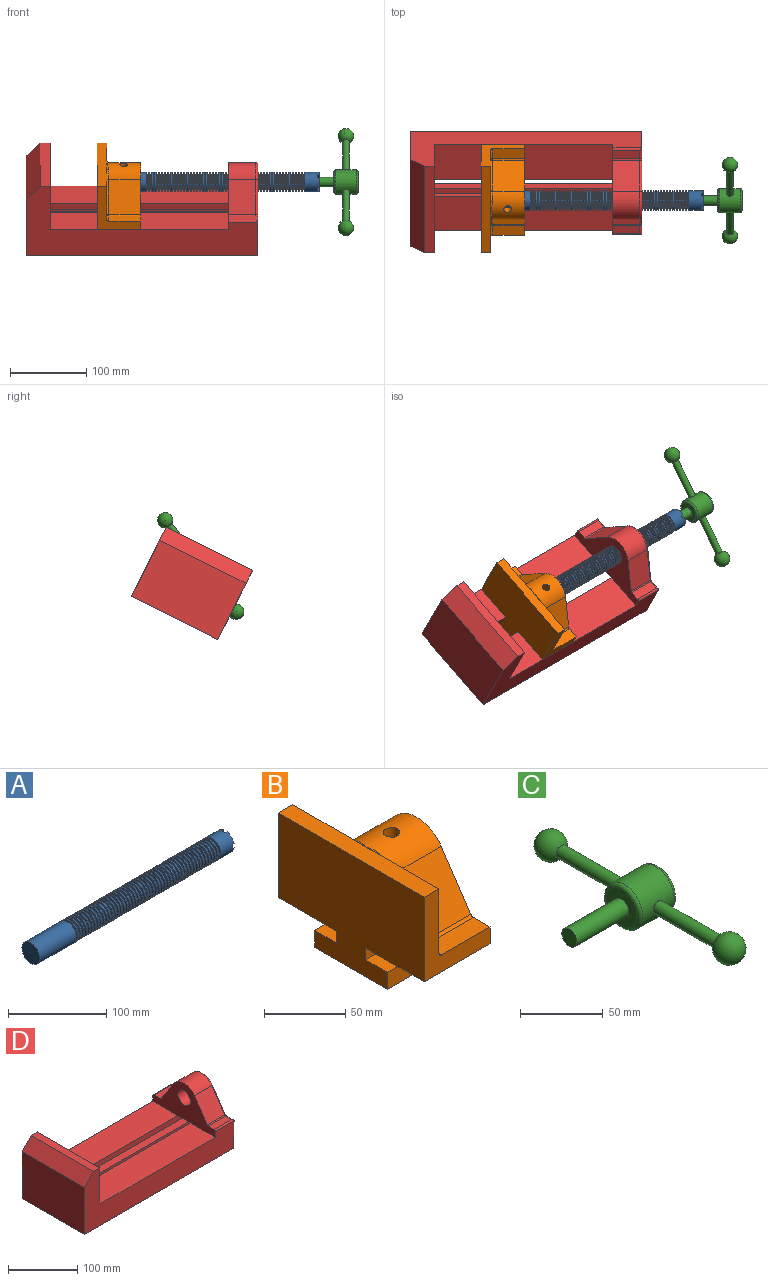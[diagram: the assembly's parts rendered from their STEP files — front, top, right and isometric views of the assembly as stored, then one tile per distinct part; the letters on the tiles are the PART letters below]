
ASSEMBLY  parts=4 mates=3
PART A: 220 faces, bbox 279.4x25.4x25.4 mm
  f0: cylinder r=12.7mm len=25.4mm, axis (-1,0,0), area 1468.2mm2, adj f1,f2,f3,f5,f7,f208,f209,f210
  f1: plane 9.9x9.9mm, normal (1,0,0), area 62.3mm2, adj f0,f4,f213,f216
  f2: plane 9.9x9.9mm, normal (1,0,0), area 62.3mm2, adj f0,f4,f210,f218
  f3: plane 9.9x9.9mm, normal (1,0,0), area 62.3mm2, adj f0,f4,f209,f212
  f4: cylinder r=6.35mm len=25.4mm, axis (1,0,0), area 960.3mm2, adj f1,f2,f3,f5,f6,f208,f209,f210
  f5: plane 9.9x9.9mm, normal (1,0,0), area 62.3mm2, adj f0,f4,f215,f217
  f6: plane 12.7x12.7mm, normal (1,0,0), area 126.7mm2, adj f4
  f7: cone r=12.7mm half-angle=76deg, axis (1,0,0), area 188mm2, adj f0,f9
  f8: cone r=10.16mm half-angle=76deg, axis (-1,0,0), area 188mm2, adj f9,f10
  f9: cylinder r=10.16mm len=20.32mm, axis (1,0,0), area 81.1mm2, adj f7,f8
  f10: cylinder r=12.7mm len=25.4mm, axis (-1,0,0), area 131.7mm2, adj f8,f11
  f11: cone r=12.7mm half-angle=76deg, axis (1,0,0), area 188mm2, adj f10,f13
  f12: cone r=10.16mm half-angle=76deg, axis (-1,0,0), area 188mm2, adj f13,f14
  f13: cylinder r=10.16mm len=20.32mm, axis (1,0,0), area 81.1mm2, adj f11,f12
  f14: cylinder r=12.7mm len=25.4mm, axis (-1,0,0), area 131.7mm2, adj f12,f15
  f15: cone r=12.7mm half-angle=76deg, axis (1,0,0), area 188mm2, adj f14,f17
  f16: cone r=10.16mm half-angle=76deg, axis (-1,0,0), area 188mm2, adj f17,f18
  f17: cylinder r=10.16mm len=20.32mm, axis (1,0,0), area 81.1mm2, adj f15,f16
  f18: cylinder r=12.7mm len=25.4mm, axis (-1,0,0), area 131.7mm2, adj f16,f19
  f19: cone r=12.7mm half-angle=76deg, axis (1,0,0), area 188mm2, adj f18,f21
  f20: cone r=10.16mm half-angle=76deg, axis (-1,0,0), area 188mm2, adj f21,f22
  f21: cylinder r=10.16mm len=20.32mm, axis (1,0,0), area 81.1mm2, adj f19,f20
  f22: cylinder r=12.7mm len=25.4mm, axis (-1,0,0), area 131.7mm2, adj f20,f23
  f23: cone r=12.7mm half-angle=76deg, axis (1,0,0), area 188mm2, adj f22,f25
  f24: cone r=10.16mm half-angle=76deg, axis (-1,0,0), area 188mm2, adj f25,f26
  f25: cylinder r=10.16mm len=20.32mm, axis (1,0,0), area 81.1mm2, adj f23,f24
  f26: cylinder r=12.7mm len=25.4mm, axis (-1,0,0), area 131.7mm2, adj f24,f27
  f27: cone r=12.7mm half-angle=76deg, axis (1,0,0), area 188mm2, adj f26,f29
  f28: cone r=10.16mm half-angle=76deg, axis (-1,0,0), area 188mm2, adj f29,f30
  f29: cylinder r=10.16mm len=20.32mm, axis (1,0,0), area 81.1mm2, adj f27,f28
  f30: cylinder r=12.7mm len=25.4mm, axis (-1,0,0), area 131.7mm2, adj f28,f31
  f31: cone r=12.7mm half-angle=76deg, axis (1,0,0), area 188mm2, adj f30,f33
  f32: cone r=10.16mm half-angle=76deg, axis (-1,0,0), area 188mm2, adj f33,f34
  f33: cylinder r=10.16mm len=20.32mm, axis (1,0,0), area 81.1mm2, adj f31,f32
  f34: cylinder r=12.7mm len=25.4mm, axis (-1,0,0), area 131.7mm2, adj f32,f35
  f35: cone r=12.7mm half-angle=76deg, axis (1,0,0), area 188mm2, adj f34,f37
  f36: cone r=10.16mm half-angle=76deg, axis (-1,0,0), area 188mm2, adj f37,f38
  f37: cylinder r=10.16mm len=20.32mm, axis (1,0,0), area 81.1mm2, adj f35,f36
  f38: cylinder r=12.7mm len=25.4mm, axis (-1,0,0), area 131.7mm2, adj f36,f39
  f39: cone r=12.7mm half-angle=76deg, axis (1,0,0), area 188mm2, adj f38,f41
  f40: cone r=10.16mm half-angle=76deg, axis (-1,0,0), area 188mm2, adj f41,f42
  f41: cylinder r=10.16mm len=20.32mm, axis (1,0,0), area 81.1mm2, adj f39,f40
  f42: cylinder r=12.7mm len=25.4mm, axis (-1,0,0), area 131.7mm2, adj f40,f43
  f43: cone r=12.7mm half-angle=76deg, axis (1,0,0), area 188mm2, adj f42,f45
  f44: cone r=10.16mm half-angle=76deg, axis (-1,0,0), area 188mm2, adj f45,f46
  f45: cylinder r=10.16mm len=20.32mm, axis (1,0,0), area 81.1mm2, adj f43,f44
  f46: cylinder r=12.7mm len=25.4mm, axis (-1,0,0), area 131.7mm2, adj f44,f47
  f47: cone r=12.7mm half-angle=76deg, axis (1,0,0), area 188mm2, adj f46,f49
  f48: cone r=10.16mm half-angle=76deg, axis (-1,0,0), area 188mm2, adj f49,f50
  f49: cylinder r=10.16mm len=20.32mm, axis (1,0,0), area 81.1mm2, adj f47,f48
  f50: cylinder r=12.7mm len=25.4mm, axis (-1,0,0), area 131.7mm2, adj f48,f51
  f51: cone r=12.7mm half-angle=76deg, axis (1,0,0), area 188mm2, adj f50,f53
  f52: cone r=10.16mm half-angle=76deg, axis (-1,0,0), area 188mm2, adj f53,f54
  f53: cylinder r=10.16mm len=20.32mm, axis (1,0,0), area 81.1mm2, adj f51,f52
  f54: cylinder r=12.7mm len=25.4mm, axis (-1,0,0), area 131.7mm2, adj f52,f55
  f55: cone r=12.7mm half-angle=76deg, axis (1,0,0), area 188mm2, adj f54,f57
  f56: cone r=10.16mm half-angle=76deg, axis (-1,0,0), area 188mm2, adj f57,f58
  f57: cylinder r=10.16mm len=20.32mm, axis (1,0,0), area 81.1mm2, adj f55,f56
  f58: cylinder r=12.7mm len=25.4mm, axis (-1,0,0), area 131.7mm2, adj f56,f59
  f59: cone r=12.7mm half-angle=76deg, axis (1,0,0), area 188mm2, adj f58,f61
  f60: cone r=10.16mm half-angle=76deg, axis (-1,0,0), area 188mm2, adj f61,f62
  f61: cylinder r=10.16mm len=20.32mm, axis (1,0,0), area 81.1mm2, adj f59,f60
  f62: cylinder r=12.7mm len=25.4mm, axis (-1,0,0), area 131.7mm2, adj f60,f63
  f63: cone r=12.7mm half-angle=76deg, axis (1,0,0), area 188mm2, adj f62,f65
  f64: cone r=10.16mm half-angle=76deg, axis (-1,0,0), area 188mm2, adj f65,f66
  f65: cylinder r=10.16mm len=20.32mm, axis (1,0,0), area 81.1mm2, adj f63,f64
  f66: cylinder r=12.7mm len=25.4mm, axis (-1,0,0), area 131.7mm2, adj f64,f67
  f67: cone r=12.7mm half-angle=76deg, axis (1,0,0), area 188mm2, adj f66,f69
  f68: cone r=10.16mm half-angle=76deg, axis (-1,0,0), area 188mm2, adj f69,f70
  f69: cylinder r=10.16mm len=20.32mm, axis (1,0,0), area 81.1mm2, adj f67,f68
  f70: cylinder r=12.7mm len=25.4mm, axis (-1,0,0), area 131.7mm2, adj f68,f71
  f71: cone r=12.7mm half-angle=76deg, axis (1,0,0), area 188mm2, adj f70,f73
  f72: cone r=10.16mm half-angle=76deg, axis (-1,0,0), area 188mm2, adj f73,f74
  f73: cylinder r=10.16mm len=20.32mm, axis (1,0,0), area 81.1mm2, adj f71,f72
  f74: cylinder r=12.7mm len=25.4mm, axis (-1,0,0), area 131.7mm2, adj f72,f75
  f75: cone r=12.7mm half-angle=76deg, axis (1,0,0), area 188mm2, adj f74,f77
  f76: cone r=10.16mm half-angle=76deg, axis (-1,0,0), area 188mm2, adj f77,f78
  f77: cylinder r=10.16mm len=20.32mm, axis (1,0,0), area 81.1mm2, adj f75,f76
  f78: cylinder r=12.7mm len=25.4mm, axis (-1,0,0), area 131.7mm2, adj f76,f79
  f79: cone r=12.7mm half-angle=76deg, axis (1,0,0), area 188mm2, adj f78,f81
  f80: cone r=10.16mm half-angle=76deg, axis (-1,0,0), area 188mm2, adj f81,f82
  f81: cylinder r=10.16mm len=20.32mm, axis (1,0,0), area 81.1mm2, adj f79,f80
  f82: cylinder r=12.7mm len=25.4mm, axis (-1,0,0), area 131.7mm2, adj f80,f83
  f83: cone r=12.7mm half-angle=76deg, axis (1,0,0), area 188mm2, adj f82,f85
  f84: cone r=10.16mm half-angle=76deg, axis (-1,0,0), area 188mm2, adj f85,f86
  f85: cylinder r=10.16mm len=20.32mm, axis (1,0,0), area 81.1mm2, adj f83,f84
  f86: cylinder r=12.7mm len=25.4mm, axis (-1,0,0), area 131.7mm2, adj f84,f87
  f87: cone r=12.7mm half-angle=76deg, axis (1,0,0), area 188mm2, adj f86,f89
  f88: cone r=10.16mm half-angle=76deg, axis (-1,0,0), area 188mm2, adj f89,f90
  f89: cylinder r=10.16mm len=20.32mm, axis (1,0,0), area 81.1mm2, adj f87,f88
  f90: cylinder r=12.7mm len=25.4mm, axis (-1,0,0), area 131.7mm2, adj f88,f91
  f91: cone r=12.7mm half-angle=76deg, axis (1,0,0), area 188mm2, adj f90,f93
  f92: cone r=10.16mm half-angle=76deg, axis (-1,0,0), area 188mm2, adj f93,f94
  f93: cylinder r=10.16mm len=20.32mm, axis (1,0,0), area 81.1mm2, adj f91,f92
  f94: cylinder r=12.7mm len=25.4mm, axis (-1,0,0), area 131.7mm2, adj f92,f95
  f95: cone r=12.7mm half-angle=76deg, axis (1,0,0), area 188mm2, adj f94,f97
  f96: cone r=10.16mm half-angle=76deg, axis (-1,0,0), area 188mm2, adj f97,f98
  f97: cylinder r=10.16mm len=20.32mm, axis (1,0,0), area 81.1mm2, adj f95,f96
  f98: cylinder r=12.7mm len=25.4mm, axis (-1,0,0), area 131.7mm2, adj f96,f99
  f99: cone r=12.7mm half-angle=76deg, axis (1,0,0), area 188mm2, adj f98,f101
  f100: cone r=10.16mm half-angle=76deg, axis (-1,0,0), area 188mm2, adj f101,f102
  f101: cylinder r=10.16mm len=20.32mm, axis (1,0,0), area 81.1mm2, adj f99,f100
  f102: cylinder r=12.7mm len=25.4mm, axis (-1,0,0), area 131.7mm2, adj f100,f103
  f103: cone r=12.7mm half-angle=76deg, axis (1,0,0), area 188mm2, adj f102,f105
  f104: cone r=10.16mm half-angle=76deg, axis (-1,0,0), area 188mm2, adj f105,f106
  f105: cylinder r=10.16mm len=20.32mm, axis (1,0,0), area 81.1mm2, adj f103,f104
  f106: cylinder r=12.7mm len=25.4mm, axis (-1,0,0), area 131.7mm2, adj f104,f107
  f107: cone r=12.7mm half-angle=76deg, axis (1,0,0), area 188mm2, adj f106,f109
  f108: cone r=10.16mm half-angle=76deg, axis (-1,0,0), area 188mm2, adj f109,f110
  f109: cylinder r=10.16mm len=20.32mm, axis (1,0,0), area 81.1mm2, adj f107,f108
  f110: cylinder r=12.7mm len=25.4mm, axis (-1,0,0), area 131.7mm2, adj f108,f111
  f111: cone r=12.7mm half-angle=76deg, axis (1,0,0), area 188mm2, adj f110,f113
  f112: cone r=10.16mm half-angle=76deg, axis (-1,0,0), area 188mm2, adj f113,f114
  f113: cylinder r=10.16mm len=20.32mm, axis (1,0,0), area 81.1mm2, adj f111,f112
  f114: cylinder r=12.7mm len=25.4mm, axis (-1,0,0), area 131.7mm2, adj f112,f115
  f115: cone r=12.7mm half-angle=76deg, axis (1,0,0), area 188mm2, adj f114,f117
  f116: cone r=10.16mm half-angle=76deg, axis (-1,0,0), area 188mm2, adj f117,f118
  f117: cylinder r=10.16mm len=20.32mm, axis (1,0,0), area 81.1mm2, adj f115,f116
  f118: cylinder r=12.7mm len=25.4mm, axis (-1,0,0), area 131.7mm2, adj f116,f119
  f119: cone r=12.7mm half-angle=76deg, axis (1,0,0), area 188mm2, adj f118,f121
  f120: cone r=10.16mm half-angle=76deg, axis (-1,0,0), area 188mm2, adj f121,f122
  f121: cylinder r=10.16mm len=20.32mm, axis (1,0,0), area 81.1mm2, adj f119,f120
  f122: cylinder r=12.7mm len=25.4mm, axis (-1,0,0), area 131.7mm2, adj f120,f123
  f123: cone r=12.7mm half-angle=76deg, axis (1,0,0), area 188mm2, adj f122,f125
  f124: cone r=10.16mm half-angle=76deg, axis (-1,0,0), area 188mm2, adj f125,f126
  f125: cylinder r=10.16mm len=20.32mm, axis (1,0,0), area 81.1mm2, adj f123,f124
  f126: cylinder r=12.7mm len=25.4mm, axis (-1,0,0), area 131.7mm2, adj f124,f127
  f127: cone r=12.7mm half-angle=76deg, axis (1,0,0), area 188mm2, adj f126,f129
  f128: cone r=10.16mm half-angle=76deg, axis (-1,0,0), area 188mm2, adj f129,f130
  f129: cylinder r=10.16mm len=20.32mm, axis (1,0,0), area 81.1mm2, adj f127,f128
  f130: cylinder r=12.7mm len=25.4mm, axis (-1,0,0), area 131.7mm2, adj f128,f131
  f131: cone r=12.7mm half-angle=76deg, axis (1,0,0), area 188mm2, adj f130,f133
  f132: cone r=10.16mm half-angle=76deg, axis (-1,0,0), area 188mm2, adj f133,f134
  f133: cylinder r=10.16mm len=20.32mm, axis (1,0,0), area 81.1mm2, adj f131,f132
  f134: cylinder r=12.7mm len=25.4mm, axis (-1,0,0), area 131.7mm2, adj f132,f135
  f135: cone r=12.7mm half-angle=76deg, axis (1,0,0), area 188mm2, adj f134,f137
  f136: cone r=10.16mm half-angle=76deg, axis (-1,0,0), area 188mm2, adj f137,f138
  f137: cylinder r=10.16mm len=20.32mm, axis (1,0,0), area 81.1mm2, adj f135,f136
  f138: cylinder r=12.7mm len=25.4mm, axis (-1,0,0), area 131.7mm2, adj f136,f139
  f139: cone r=12.7mm half-angle=76deg, axis (1,0,0), area 188mm2, adj f138,f141
  f140: cone r=10.16mm half-angle=76deg, axis (-1,0,0), area 188mm2, adj f141,f142
  f141: cylinder r=10.16mm len=20.32mm, axis (1,0,0), area 81.1mm2, adj f139,f140
  f142: cylinder r=12.7mm len=25.4mm, axis (-1,0,0), area 131.7mm2, adj f140,f143
  f143: cone r=12.7mm half-angle=76deg, axis (1,0,0), area 188mm2, adj f142,f145
  f144: cone r=10.16mm half-angle=76deg, axis (-1,0,0), area 188mm2, adj f145,f146
  f145: cylinder r=10.16mm len=20.32mm, axis (1,0,0), area 81.1mm2, adj f143,f144
  f146: cylinder r=12.7mm len=25.4mm, axis (-1,0,0), area 131.7mm2, adj f144,f147
  f147: cone r=12.7mm half-angle=76deg, axis (1,0,0), area 188mm2, adj f146,f149
  f148: cone r=10.16mm half-angle=76deg, axis (-1,0,0), area 188mm2, adj f149,f150
  f149: cylinder r=10.16mm len=20.32mm, axis (1,0,0), area 81.1mm2, adj f147,f148
  f150: cylinder r=12.7mm len=25.4mm, axis (-1,0,0), area 131.7mm2, adj f148,f151
  f151: cone r=12.7mm half-angle=76deg, axis (1,0,0), area 188mm2, adj f150,f153
  f152: cone r=10.16mm half-angle=76deg, axis (-1,0,0), area 188mm2, adj f153,f154
  f153: cylinder r=10.16mm len=20.32mm, axis (1,0,0), area 81.1mm2, adj f151,f152
  f154: cylinder r=12.7mm len=25.4mm, axis (-1,0,0), area 131.7mm2, adj f152,f155
  f155: cone r=12.7mm half-angle=76deg, axis (1,0,0), area 188mm2, adj f154,f157
  f156: cone r=10.16mm half-angle=76deg, axis (-1,0,0), area 188mm2, adj f157,f158
  f157: cylinder r=10.16mm len=20.32mm, axis (1,0,0), area 81.1mm2, adj f155,f156
  f158: cylinder r=12.7mm len=25.4mm, axis (-1,0,0), area 131.7mm2, adj f156,f159
  f159: cone r=12.7mm half-angle=76deg, axis (1,0,0), area 188mm2, adj f158,f161
  f160: cone r=10.16mm half-angle=76deg, axis (-1,0,0), area 188mm2, adj f161,f162
  f161: cylinder r=10.16mm len=20.32mm, axis (1,0,0), area 81.1mm2, adj f159,f160
  f162: cylinder r=12.7mm len=25.4mm, axis (-1,0,0), area 131.7mm2, adj f160,f163
  f163: cone r=12.7mm half-angle=76deg, axis (1,0,0), area 188mm2, adj f162,f165
  f164: cone r=10.16mm half-angle=76deg, axis (-1,0,0), area 188mm2, adj f165,f166
  f165: cylinder r=10.16mm len=20.32mm, axis (1,0,0), area 81.1mm2, adj f163,f164
  f166: cylinder r=12.7mm len=25.4mm, axis (-1,0,0), area 131.7mm2, adj f164,f167
  f167: cone r=12.7mm half-angle=76deg, axis (1,0,0), area 188mm2, adj f166,f169
  f168: cone r=10.16mm half-angle=76deg, axis (-1,0,0), area 188mm2, adj f169,f170
  f169: cylinder r=10.16mm len=20.32mm, axis (1,0,0), area 81.1mm2, adj f167,f168
  f170: cylinder r=12.7mm len=25.4mm, axis (-1,0,0), area 131.7mm2, adj f168,f171
  f171: cone r=12.7mm half-angle=76deg, axis (1,0,0), area 188mm2, adj f170,f173
  f172: cone r=10.16mm half-angle=76deg, axis (-1,0,0), area 188mm2, adj f173,f174
  f173: cylinder r=10.16mm len=20.32mm, axis (1,0,0), area 81.1mm2, adj f171,f172
  f174: cylinder r=12.7mm len=25.4mm, axis (-1,0,0), area 131.7mm2, adj f172,f175
  f175: cone r=12.7mm half-angle=76deg, axis (1,0,0), area 188mm2, adj f174,f177
  f176: cone r=10.16mm half-angle=76deg, axis (-1,0,0), area 188mm2, adj f177,f178
  f177: cylinder r=10.16mm len=20.32mm, axis (1,0,0), area 81.1mm2, adj f175,f176
  f178: cylinder r=12.7mm len=25.4mm, axis (-1,0,0), area 131.7mm2, adj f176,f179
  f179: cone r=12.7mm half-angle=76deg, axis (1,0,0), area 188mm2, adj f178,f181
  f180: cone r=10.16mm half-angle=76deg, axis (-1,0,0), area 188mm2, adj f181,f182
  f181: cylinder r=10.16mm len=20.32mm, axis (1,0,0), area 81.1mm2, adj f179,f180
  f182: cylinder r=12.7mm len=25.4mm, axis (-1,0,0), area 131.7mm2, adj f180,f183
  f183: cone r=12.7mm half-angle=76deg, axis (1,0,0), area 188mm2, adj f182,f185
  f184: cone r=10.16mm half-angle=76deg, axis (-1,0,0), area 188mm2, adj f185,f186
  f185: cylinder r=10.16mm len=20.32mm, axis (1,0,0), area 81.1mm2, adj f183,f184
  f186: cylinder r=12.7mm len=25.4mm, axis (-1,0,0), area 131.7mm2, adj f184,f187
  f187: cone r=12.7mm half-angle=76deg, axis (1,0,0), area 188mm2, adj f186,f189
  f188: cone r=10.16mm half-angle=76deg, axis (-1,0,0), area 188mm2, adj f189,f190
  f189: cylinder r=10.16mm len=20.32mm, axis (1,0,0), area 81.1mm2, adj f187,f188
  f190: cylinder r=12.7mm len=25.4mm, axis (-1,0,0), area 131.7mm2, adj f188,f191
  f191: cone r=12.7mm half-angle=76deg, axis (1,0,0), area 188mm2, adj f190,f193
  f192: cone r=10.16mm half-angle=76deg, axis (-1,0,0), area 188mm2, adj f193,f194
  f193: cylinder r=10.16mm len=20.32mm, axis (1,0,0), area 81.1mm2, adj f191,f192
  f194: cylinder r=12.7mm len=25.4mm, axis (-1,0,0), area 131.7mm2, adj f192,f195
  f195: cone r=12.7mm half-angle=76deg, axis (1,0,0), area 188mm2, adj f194,f197
  f196: cone r=10.16mm half-angle=76deg, axis (-1,0,0), area 188mm2, adj f197,f198
  f197: cylinder r=10.16mm len=20.32mm, axis (1,0,0), area 81.1mm2, adj f195,f196
  f198: cylinder r=12.7mm len=25.4mm, axis (-1,0,0), area 131.7mm2, adj f196,f199
  f199: cone r=12.7mm half-angle=76deg, axis (1,0,0), area 188mm2, adj f198,f201
  f200: cone r=10.16mm half-angle=76deg, axis (-1,0,0), area 188mm2, adj f201,f202
  f201: cylinder r=10.16mm len=20.32mm, axis (1,0,0), area 81.1mm2, adj f199,f200
  f202: cylinder r=12.7mm len=25.4mm, axis (-1,0,0), area 131.7mm2, adj f200,f203
  f203: cone r=12.7mm half-angle=76deg, axis (1,0,0), area 188mm2, adj f202,f205
  f204: cone r=10.16mm half-angle=76deg, axis (-1,0,0), area 188mm2, adj f205,f207
  f205: cylinder r=10.16mm len=20.32mm, axis (1,0,0), area 81.1mm2, adj f203,f204
  f206: plane 25.4x25.4mm, normal (-1,0,0), area 506.7mm2, adj f207
  f207: cylinder r=12.7mm len=52.45mm, axis (-1,0,0), area 4185.4mm2, adj f204,f206
  f208: plane 6.88x5.08mm, normal (1,0,0), area 32.7mm2, adj f0,f4,f209,f210
  f209: plane 6.62x2.54mm, normal (0,-1,0), area 16.8mm2, adj f0,f3,f4,f208
  f210: plane 6.62x2.54mm, normal (0,1,0), area 16.8mm2, adj f0,f2,f4,f208
  f211: plane 6.88x5.08mm, normal (1,0,0), area 32.7mm2, adj f0,f4,f212,f213
  f212: plane 6.62x2.54mm, normal (0,0,1), area 16.8mm2, adj f0,f3,f4,f211
  f213: plane 6.62x2.54mm, normal (0,0,-1), area 16.8mm2, adj f0,f1,f4,f211
  f214: plane 6.88x5.08mm, normal (1,0,0), area 32.7mm2, adj f0,f4,f215,f216
  f215: plane 6.62x2.54mm, normal (0,1,0), area 16.8mm2, adj f0,f4,f5,f214
  f216: plane 6.62x2.54mm, normal (0,-1,0), area 16.8mm2, adj f0,f1,f4,f214
  f217: plane 6.62x2.54mm, normal (0,0,-1), area 16.8mm2, adj f0,f4,f5,f219
  f218: plane 6.62x2.54mm, normal (0,0,1), area 16.8mm2, adj f0,f2,f4,f219
  f219: plane 6.88x5.08mm, normal (1,0,0), area 32.7mm2, adj f0,f4,f217,f218
PART B: 36 faces, bbox 57.2x127x89 mm
  f0: plane 57.15x50.8mm, normal (0,0,-1), area 2903.2mm2, adj f6,f9,f10,f23
  f1: cylinder r=12.7mm len=44.45mm, axis (1,0,0), area 3464.3mm2, adj f6,f15,f16
  f2: plane 41.91x14.52mm, normal (0,0,1), area 608.5mm2, adj f6,f11,f24,f25
  f3: plane 51.86x48.26mm, normal (1,0,0), area 1495.7mm2, adj f8,f10,f31,f33,f35
  f4: plane 51.86x48.26mm, normal (1,0,0), area 1495.7mm2, adj f8,f11,f24,f28,f29
  f5: plane 57.15x50.8mm, normal (0,0,-1), area 2903.2mm2, adj f6,f9,f11,f22
  f6: plane 127x85.09mm, normal (1,0,0), area 5190.6mm2, adj f0,f1,f2,f5,f7,f10,f11,f12
  f7: plane 41.91x14.52mm, normal (0,0,1), area 608.5mm2, adj f6,f10,f30,f31
  f8: plane 127x12.7mm, normal (0,0,1), area 1612.9mm2, adj f3,f4,f9,f10,f11,f26,f34
  f9: plane 127x85.09mm, normal (-1,0,0), area 9096.8mm2, adj f0,f5,f8,f10,f11,f17,f18,f19
  f10: plane 63.5x57.15mm, normal (0,-1,0), area 1372.3mm2, adj f0,f3,f6,f7,f8,f9,f31
  f11: plane 63.5x57.15mm, normal (0,1,0), area 1372.3mm2, adj f2,f4,f5,f6,f8,f9,f24
  f12: plane 41.91x38.43mm, normal (0,-0.83,0.56), area 1939.2mm2, adj f6,f13,f30,f33
  f13: cylinder r=25.4mm len=44.45mm, axis (1,0,0), area 2026.5mm2, adj f6,f12,f14,f16,f26,f28,f34,f35
  f14: plane 41.91x38.43mm, normal (0,0.83,0.56), area 1939.2mm2, adj f6,f13,f25,f29
  f15: plane 25.4x25.4mm, normal (1,0,0), area 506.7mm2, adj f1
  f16: cylinder r=5.08mm len=13.76mm, axis (0,0,1), area 414mm2, adj f1,f13
  f17: plane 57.15x19.05mm, normal (0,0,1), area 1088.7mm2, adj f6,f9,f18,f23
  f18: plane 57.15x12.7mm, normal (0,-1,0), area 725.8mm2, adj f6,f9,f17,f19
  f19: plane 63.5x57.15mm, normal (0,0,-1), area 3629mm2, adj f6,f9,f18,f20
  f20: plane 57.15x12.7mm, normal (0,1,0), area 725.8mm2, adj f6,f9,f19,f21
  f21: plane 57.15x19.05mm, normal (0,0,1), area 1088.7mm2, adj f6,f9,f20,f22
  f22: plane 57.15x8.89mm, normal (0,1,0), area 508.1mm2, adj f5,f6,f9,f21
  f23: plane 57.15x8.89mm, normal (0,-1,0), area 508.1mm2, adj f0,f6,f9,f17
  f24: cylinder r=2.54mm len=14.52mm, axis (0,-1,0), area 57.9mm2, adj f2,f4,f11,f27
  f25: cylinder r=2.54mm len=41.91mm, axis (1,0,0), area 104.3mm2, adj f2,f6,f14,f27
  f26: bspline ~12.24x2.8mm, area 20.9mm2, adj f8,f13,f28
  f27: sphere r=2.54mm, area 6.3mm2, adj f24,f25,f29
  f28: torus R=27.94mm, axis (1,0,0), area 57.8mm2, adj f4,f13,f26,f29
  f29: cylinder r=2.54mm len=39.84mm, axis (0,-0.56,0.83), area 184.6mm2, adj f4,f14,f27,f28
  f30: cylinder r=2.54mm len=41.91mm, axis (1,0,0), area 104.3mm2, adj f6,f7,f12,f32
  f31: cylinder r=2.54mm len=14.52mm, axis (0,-1,0), area 57.9mm2, adj f3,f7,f10,f32
  f32: sphere r=2.54mm, area 6.3mm2, adj f30,f31,f33
  f33: cylinder r=2.54mm len=39.84mm, axis (0,-0.56,-0.83), area 184.6mm2, adj f3,f12,f32,f35
  f34: bspline ~12.24x2.8mm, area 20.9mm2, adj f8,f13,f35
  f35: torus R=27.94mm, axis (1,0,0), area 57.8mm2, adj f3,f13,f33,f34
PART C: 11 faces, bbox 76.2x172.7x34.4 mm
  f0: sphere r=10.16mm, area 1231.8mm2, adj f1
  f1: cylinder r=4.45mm len=51.82mm, axis (0,1,0), area 1438.5mm2, adj f0,f4
  f2: sphere r=10.16mm, area 1231.8mm2, adj f3
  f3: cylinder r=4.45mm len=51.82mm, axis (0,1,0), area 1438.5mm2, adj f2,f4
  f4: cylinder r=15.88mm len=31.75mm, axis (-1,0,0), area 2534.7mm2, adj f1,f3,f9,f10
  f5: cylinder r=6.35mm len=44.45mm, axis (-1,0,0), area 1773.5mm2, adj f6,f8
  f6: plane 12.7x12.7mm, normal (-1,0,0), area 126.7mm2, adj f5
  f7: plane 26.67x26.67mm, normal (1,0,0), area 558.6mm2, adj f10
  f8: plane 26.67x26.67mm, normal (-1,0,0), area 432mm2, adj f5,f9
  f9: torus R=13.33mm, axis (1,0,0), area 374.8mm2, adj f4,f8
  f10: torus R=13.33mm, axis (1,0,0), area 374.8mm2, adj f4,f7
PART D: 39 faces, bbox 304.8x127x103.7 mm
  f0: plane 234.95x50.8mm, normal (0,0,1), area 11935.5mm2, adj f3,f8,f16,f26
  f1: plane 127x99.06mm, normal (1,0,0), area 7097.5mm2, adj f7,f8,f9,f14,f17,f18,f19,f20
  f2: plane 234.95x50.8mm, normal (0,0,1), area 11935.5mm2, adj f3,f9,f16,f27
  f3: plane 127x101.6mm, normal (1,0,0), area 9516.1mm2, adj f0,f2,f4,f7,f8,f9,f18,f19
  f4: plane 127x12.7mm, normal (0,0,1), area 1612.9mm2, adj f3,f5,f8,f9
  f5: plane 127x19.05mm, normal (-0.71,0,0.71), area 3421.5mm2, adj f4,f6,f8,f9
  f6: plane 127x82.55mm, normal (-1,0,0), area 10483.8mm2, adj f5,f7,f8,f9
  f7: plane 304.8x127mm, normal (0,0,-1), area 31774.1mm2, adj f1,f3,f6,f8,f9,f21,f22
  f8: plane 304.8x101.6mm, normal (0,-1,0), area 13834.6mm2, adj f0,f1,f3,f4,f5,f6,f7,f16
  f9: plane 304.8x101.6mm, normal (0,1,0), area 13834.6mm2, adj f1,f2,f3,f4,f5,f6,f7,f16
  f10: plane 35.56x11.98mm, normal (0,0,1), area 426mm2, adj f16,f28,f29,f30
  f11: plane 38.43x35.56mm, normal (0,0.83,0.56), area 1645.4mm2, adj f12,f16,f29,f32
  f12: cylinder r=25.4mm len=42.19mm, axis (1,0,0), area 1770.2mm2, adj f11,f13,f16,f33
  f13: plane 38.43x35.56mm, normal (0,-0.83,0.56), area 1645.4mm2, adj f12,f16,f34,f35
  f14: cylinder r=12.7mm len=38.1mm, axis (1,0,0), area 3040.2mm2, adj f1,f16
  f15: plane 35.56x11.98mm, normal (0,0,1), area 426mm2, adj f16,f34,f36,f38
  f16: plane 127x63.5mm, normal (-1,0,0), area 4155.5mm2, adj f0,f2,f8,f9,f10,f11,f12,f13
  f17: plane 38.1x25.4mm, normal (0,0,-1), area 967.7mm2, adj f1,f16,f26,f27
  f18: plane 273.05x19.05mm, normal (0,0,-1), area 5201.6mm2, adj f1,f3,f19,f26
  f19: plane 273.05x12.7mm, normal (0,1,0), area 3467.7mm2, adj f1,f3,f18,f20
  f20: plane 273.05x19.05mm, normal (0,0,1), area 5201.6mm2, adj f1,f3,f19,f21
  f21: plane 273.05x16.51mm, normal (0,1,0), area 4508.1mm2, adj f1,f3,f7,f20
  f22: plane 273.05x16.51mm, normal (0,-1,0), area 4508.1mm2, adj f1,f3,f7,f23
  f23: plane 273.05x19.05mm, normal (0,0,1), area 5201.6mm2, adj f1,f3,f22,f24
  f24: plane 273.05x12.7mm, normal (0,-1,0), area 3467.7mm2, adj f1,f3,f23,f25
  f25: plane 273.05x19.05mm, normal (0,0,-1), area 5201.6mm2, adj f1,f3,f24,f27
  f26: plane 273.05x8.89mm, normal (0,1,0), area 2427.4mm2, adj f0,f1,f3,f17,f18
  f27: plane 273.05x8.89mm, normal (0,-1,0), area 2427.4mm2, adj f1,f2,f3,f17,f25
  f28: cylinder r=2.54mm len=38.1mm, axis (1,0,0), area 148.3mm2, adj f9,f10,f16,f30
  f29: cylinder r=2.54mm len=35.56mm, axis (-1,0,0), area 88.5mm2, adj f10,f11,f16,f31
  f30: cylinder r=2.54mm len=14.52mm, axis (0,1,0), area 54.3mm2, adj f1,f10,f28,f31
  f31: torus R=5.08mm, axis (-1,0,0), area 13.5mm2, adj f1,f29,f30,f32
  f32: cylinder r=2.54mm len=39.84mm, axis (0,0.56,-0.83), area 184.6mm2, adj f1,f11,f31,f33
  f33: torus R=22.86mm, axis (-1,0,0), area 191.4mm2, adj f1,f12,f32,f35
  f34: cylinder r=2.54mm len=35.56mm, axis (-1,0,0), area 88.5mm2, adj f13,f15,f16,f37
  f35: cylinder r=2.54mm len=39.84mm, axis (0,0.56,0.83), area 184.6mm2, adj f1,f13,f33,f37
  f36: cylinder r=2.54mm len=38.1mm, axis (-1,0,0), area 148.3mm2, adj f8,f15,f16,f38
  f37: torus R=5.08mm, axis (-1,0,0), area 13.5mm2, adj f1,f34,f35,f38
  f38: cylinder r=2.54mm len=14.52mm, axis (0,1,0), area 54.3mm2, adj f1,f15,f36,f37
PLACE A rot(axis=(-1,0,0),127.8deg) t=(61.68,396.22,-42.7)mm
PLACE B rot(axis=(1,0,0),26.7deg) t=(61.68,490.71,-157.42)mm
PLACE C rot(axis=(-1,0,0),127.8deg) t=(61.68,396.22,-42.7)mm
PLACE D rot(axis=(1,0,0),26.7deg) t=(0,490.71,-157.42)mm fixed
MATE fastened A.f7 <-> C.f5  axis (1,0,0) through (55.33,456.46,-89.36)mm
MATE revolute B.f28 <-> A.f7  axis (1,0,0) through (-198.67,456.46,-89.36)mm
MATE slider B.f9 <-> D.f3  axis (-1,0,0) through (-211.37,416.87,-151.93)mm
